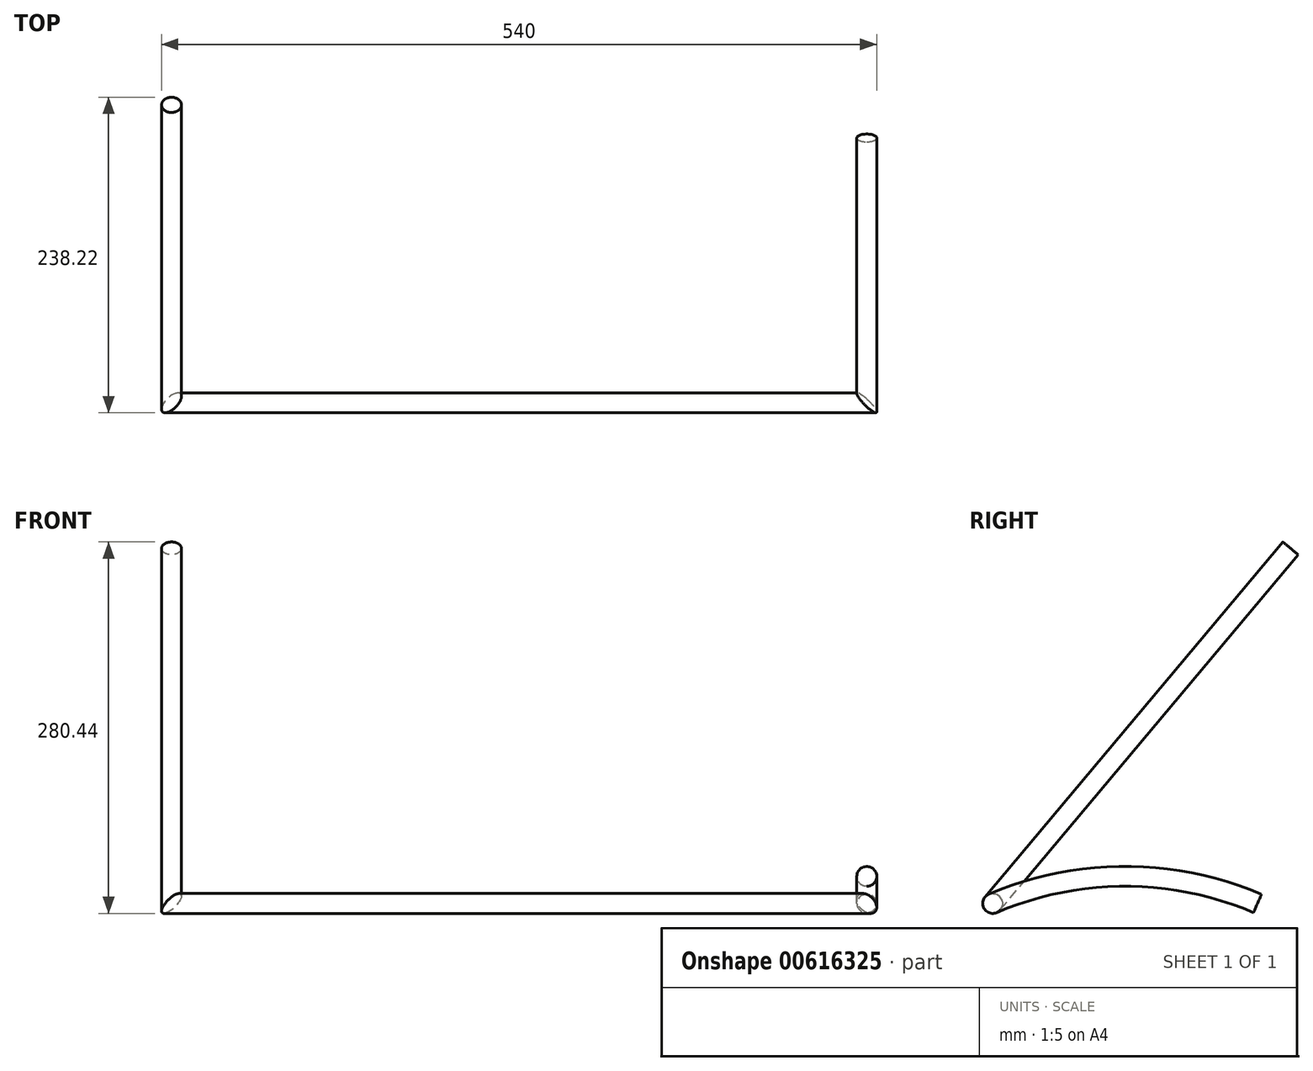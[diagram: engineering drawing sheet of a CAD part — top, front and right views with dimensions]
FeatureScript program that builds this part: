
annotation { "Feature Type Name" : "Feature", "Feature Type Description" : "" }
export const myFeature = defineFeature(function(context is Context, id is Id, definition is map)
    precondition{}
    {
        {
            var Q0;
            Q0=qCreatedBy(makeId("Front.planeOp"),FACE);
            cPlane(context, id + "F0", {"entities" : qUnion([Q0]), "cplaneType" : CPlaneType.OFFSET, "offset" : 100 * mm, "width" : 150 * mm, "height" : 150 * mm});
        }
        {
            var Q0;
            Q0=qCreatedBy(id+"F0.planeOp",FACE);
            var sketch = newSketch(context, id + "F1", { "sketchPlane" : qUnion([Q0])});
            skLineSegment(sketch, "E0", {"start": v(0, -200) * mm, "end": v(-525, -200) * mm});
            skSolve(sketch);
        }
        {
            var Q0;
            Q0=qCreatedBy(makeId("Right.planeOp"),FACE);
            cPlane(context, id + "F2", {"entities" : qUnion([Q0]), "cplaneType" : CPlaneType.OFFSET, "offset" : 525 * mm, "oppositeDirection" : true, "width" : 150 * mm, "height" : 150 * mm});
        }
        {
            var Q0;
            Q0=qCreatedBy(id+"F2.planeOp",FACE);
            var sketch = newSketch(context, id + "F3", { "sketchPlane" : qUnion([Q0])});
            skLineSegment(sketch, "E1", {"start": v(-100, -200) * mm, "end": v(124.98, 68.12) * mm});
            skSolve(sketch);
        }
        {
            var Q0;
            Q0=qCreatedBy(makeId("Right.planeOp"),FACE);
            var sketch = newSketch(context, id + "F4", { "sketchPlane" : qUnion([Q0])});
            skArc(sketch, "E2", {"start": v(100, -200) * mm, "mid": v(0, -179.57) * mm, "end": v(-100, -200) * mm});
            skSolve(sketch);
        }
        {
            var Q0;
            Q0=qCreatedBy(makeId("Front.planeOp"),FACE);
            var sketch = newSketch(context, id + "F5", { "sketchPlane" : qUnion([Q0])});
            skCircle(sketch, "E3", {"center": v(0, -179.57) * mm, "radius": 7.5 * mm});
            skSolve(sketch);
        }
        {
            var Q0;
            Q0=makeQuery(id+"F5.imprint","IMPRINT",FACE,{"disambiguationData":[TD([[makeQuery(id+"F5.imprint","IMPRINT",EDGE,{"derivedFrom":sQuery(id+"F5.wireOp",EDGE,"E3")}),1.0]])]});
            var Q1;
            Q1=sQuery(id+"F1.wireOp",EDGE,"E0");
            var Q2;
            Q2=sQuery(id+"F4.wireOp",EDGE,"E2");
            var Q3;
            Q3=sQuery(id+"F3.wireOp",EDGE,"E1");
            sweep(context, id + "F6", {"profiles" : qUnion([Q0]), "path" : qUnion([Q1, Q2, Q3])});
        }
    });
